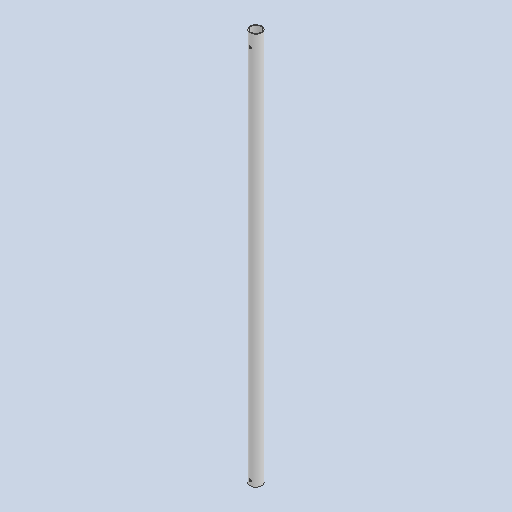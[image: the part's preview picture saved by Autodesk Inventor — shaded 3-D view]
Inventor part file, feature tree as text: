
AUTODESK INVENTOR PART (.ipt)
format: ipt  version: 2022 (Build 260153000, 153)  size: 174,592 bytes
history: native  units: mm
features: extrude x2, sketch x2
ambient origin geometry x8: Origin, YZ Plane, XZ Plane, XY Plane, X Axis, Y Axis, Z Axis, Center Point
bodies: Body1 (feature_tree)
feature tree (4):
  extrude  "Extrusion5"  Depth=15.0mm
  extrude  "Extrusion6"  Depth=10.0mm TaperAngle=0.0deg
  sketch  "Sketch2"  dims[d31=34.456mm d91=15.0mm]
  sketch  "Sketch3"  dims[d92=13.0mm d93=500.0mm d94=0.0mm d95=6.0mm d96=3.0mm d97=20.0mm d98=10.0mm d99=0.0mm d100=0.0mm d101=16.0mm d102=3.0mm]
